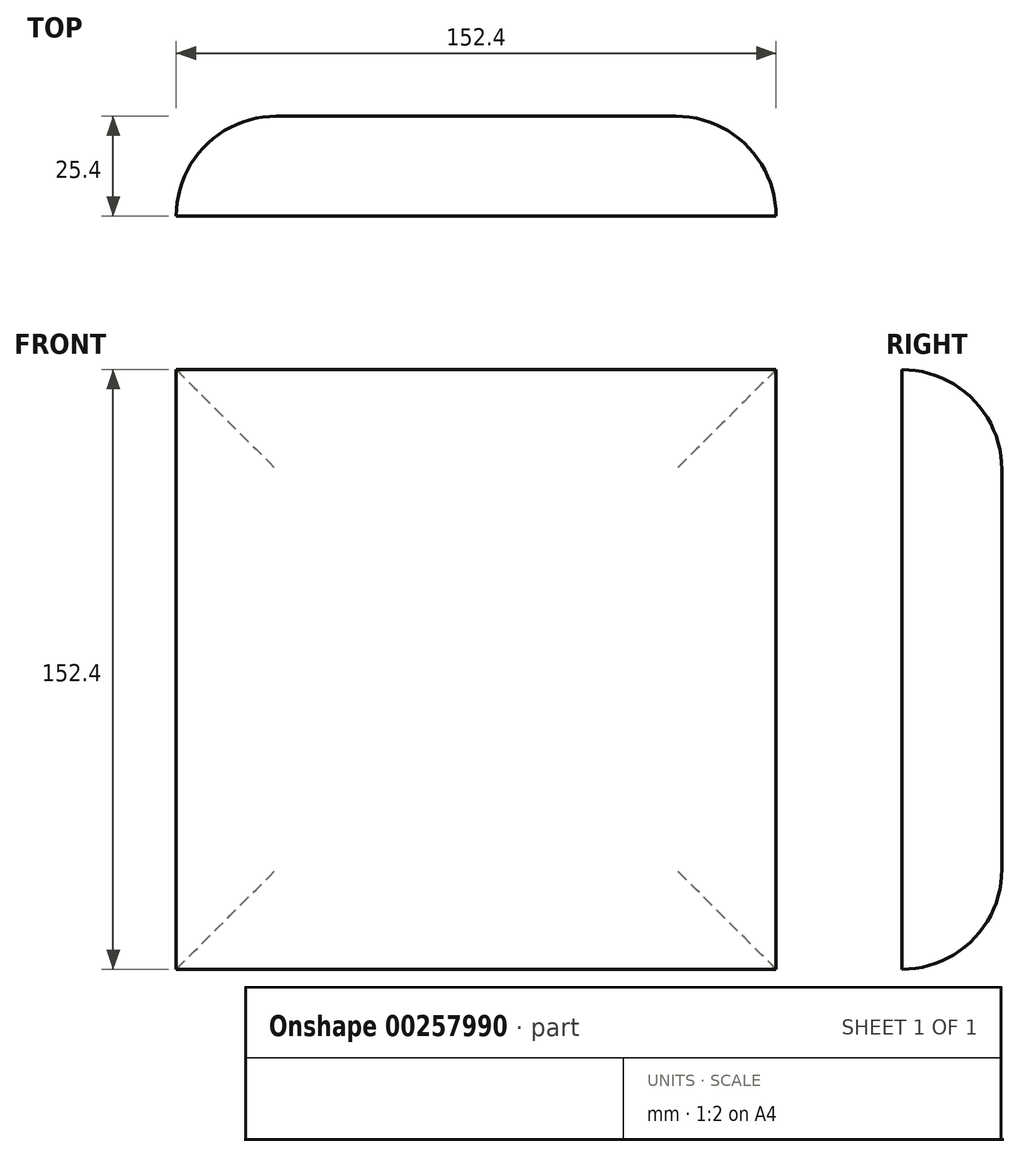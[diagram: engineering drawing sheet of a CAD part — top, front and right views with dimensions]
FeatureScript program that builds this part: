
annotation { "Feature Type Name" : "Feature", "Feature Type Description" : "" }
export const myFeature = defineFeature(function(context is Context, id is Id, definition is map)
    precondition{}
    {
        {
            var Q0;
            Q0=qCreatedBy(makeId("Front.planeOp"),FACE);
            var sketch = newSketch(context, id + "F0", { "sketchPlane" : qUnion([Q0])});
            skLineSegment(sketch, "E0.bottom", {"start": v(72.41, 76.2) * mm, "end": v(-79.99, 76.2) * mm});
            skLineSegment(sketch, "E0.top", {"start": v(72.41, -76.2) * mm, "end": v(-79.99, -76.2) * mm});
            skLineSegment(sketch, "E0.left", {"start": v(72.41, 76.2) * mm, "end": v(72.41, -76.2) * mm});
            skLineSegment(sketch, "E0.right", {"start": v(-79.99, 76.2) * mm, "end": v(-79.99, -76.2) * mm});
            skPoint(sketch, "E0.middle", {"position": v(-3.79, 0) * mm});
            skSolve(sketch);
        }
        {
            var Q0;
            Q0=makeQuery(id+"F0.imprint","IMPRINT",FACE,{"disambiguationData":[TD([[makeQuery(id+"F0.imprint","IMPRINT",EDGE,{"derivedFrom":sQuery(id+"F0.wireOp",EDGE,"E0.bottom")}),1.0]])]});
            extrude(context, id + "F1", {"entities" : qUnion([Q0]), "depth" : 25.4 * mm});
        }
        {
            var Q0;
            Q0=makeQuery(id+"F1.opExtrude","CAP_FACE",FACE,{"disambiguationData":[OSD([sQuery(id+"F0.wireOp",EDGE,"E0.bottom"),sQuery(id+"F0.wireOp",EDGE,"E0.top"),sQuery(id+"F0.wireOp",EDGE,"E0.left"),sQuery(id+"F0.wireOp",EDGE,"E0.right")])],"isStart":true});
            fillet(context, id + "F2", {"entities" : qUnion([Q0]), "radius" : 25.4 * mm, "tangentPropagation" : true, "allowEdgeOverflow" : false});
        }
    });
